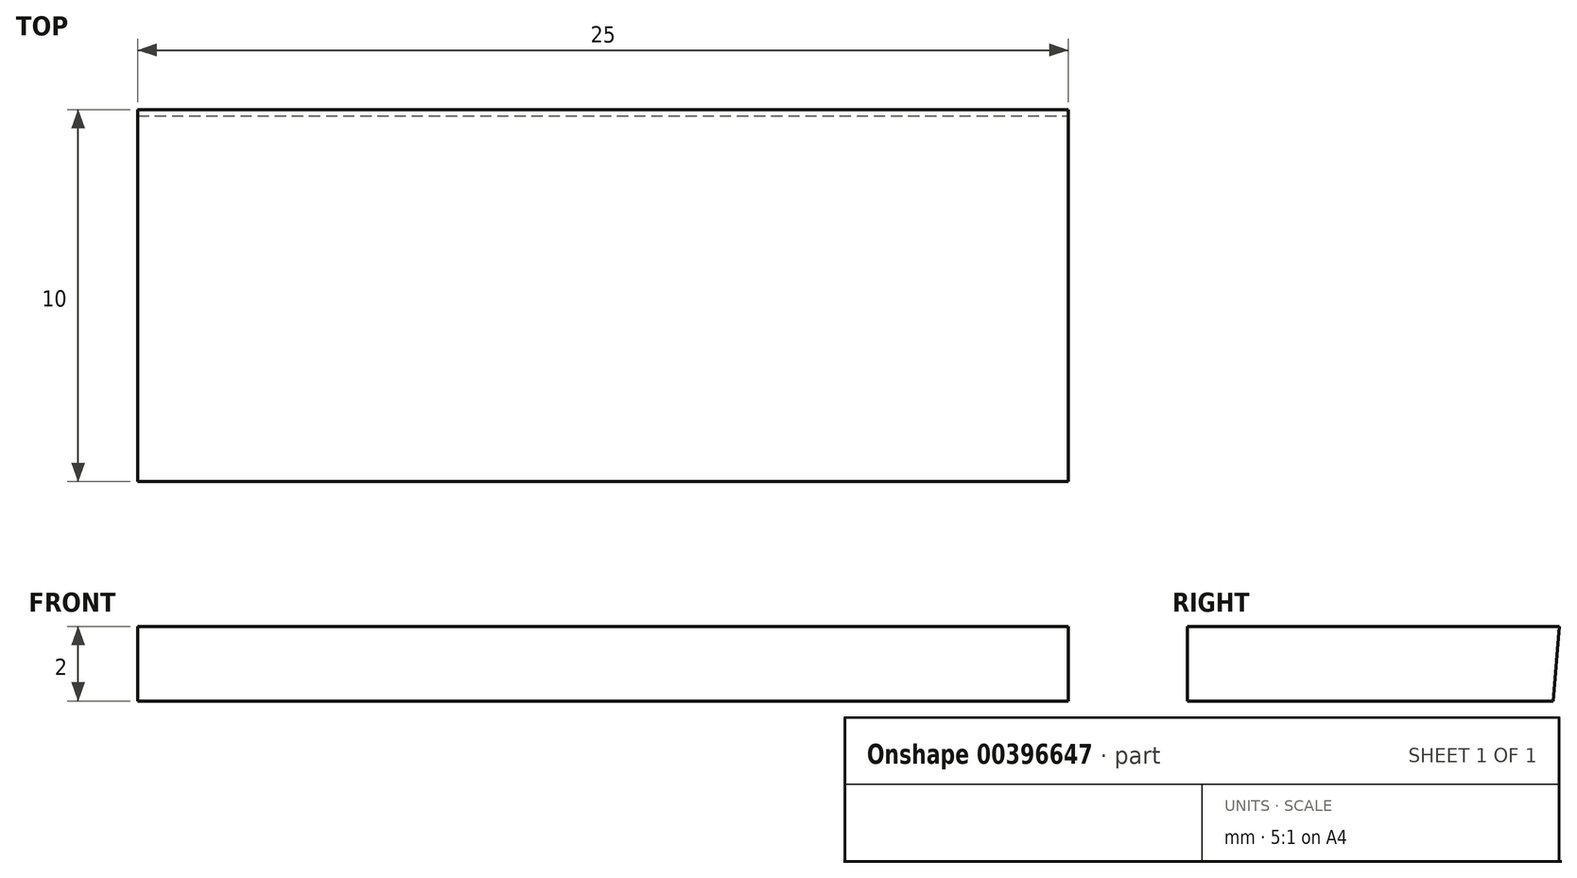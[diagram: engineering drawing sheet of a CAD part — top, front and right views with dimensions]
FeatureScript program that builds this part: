
annotation { "Feature Type Name" : "Feature", "Feature Type Description" : "" }
export const myFeature = defineFeature(function(context is Context, id is Id, definition is map)
    precondition{}
    {
        {
            var Q0;
            Q0=qCreatedBy(makeId("Top.planeOp"),FACE);
            var sketch = newSketch(context, id + "F0", { "sketchPlane" : qUnion([Q0])});
            skLineSegment(sketch, "E0.bottom", {"start": v(12.5, 5) * mm, "end": v(-12.5, 5) * mm});
            skLineSegment(sketch, "E0.top", {"start": v(12.5, -5) * mm, "end": v(-12.5, -5) * mm});
            skLineSegment(sketch, "E0.left", {"start": v(12.5, 5) * mm, "end": v(12.5, -5) * mm});
            skLineSegment(sketch, "E0.right", {"start": v(-12.5, 5) * mm, "end": v(-12.5, -5) * mm});
            skPoint(sketch, "E0.middle", {"position": v(0, 0) * mm});
            skSolve(sketch);
        }
        {
            var Q0;
            Q0 = qSketchRegion(id + "F0", true);
            extrude(context, id + "F1", {"entities" : qUnion([Q0]), "depth" : 2 * mm});
        }
        {
            var Q0;
            Q0=makeQuery(id+"F1.opExtrude","SWEPT_FACE",FACE,{"disambiguationData":[OSD([sQuery(id+"F0.wireOp",EDGE,"E0.left")])]});
            var sketch = newSketch(context, id + "F2", { "sketchPlane" : qUnion([Q0])});
            skLineSegment(sketch, "E1", {"start": v(5, 0) * mm, "end": v(4.83, 0) * mm});
            skLineSegment(sketch, "E2", {"start": v(4.83, 0) * mm, "end": v(5, 2) * mm});
            skLineSegment(sketch, "E3", {"start": v(5, 2) * mm, "end": v(5, 0) * mm});
            skSolve(sketch);
        }
        {
            var Q0;
            Q0=makeQuery(id+"F2.imprint","IMPRINT",FACE,{"disambiguationData":[TD([[makeQuery(id+"F2.imprint","IMPRINT",EDGE,{"derivedFrom":sQuery(id+"F2.wireOp",EDGE,"E1")}),-1.0]])]});
            extrude(context, id + "F3", {"entities" : qUnion([Q0]), "operationType" : NewBodyOperationType.REMOVE, "endBound" : BoundingType.UP_TO_NEXT, "oppositeDirection" : true, "depth" : 25 * mm});
        }
    });
